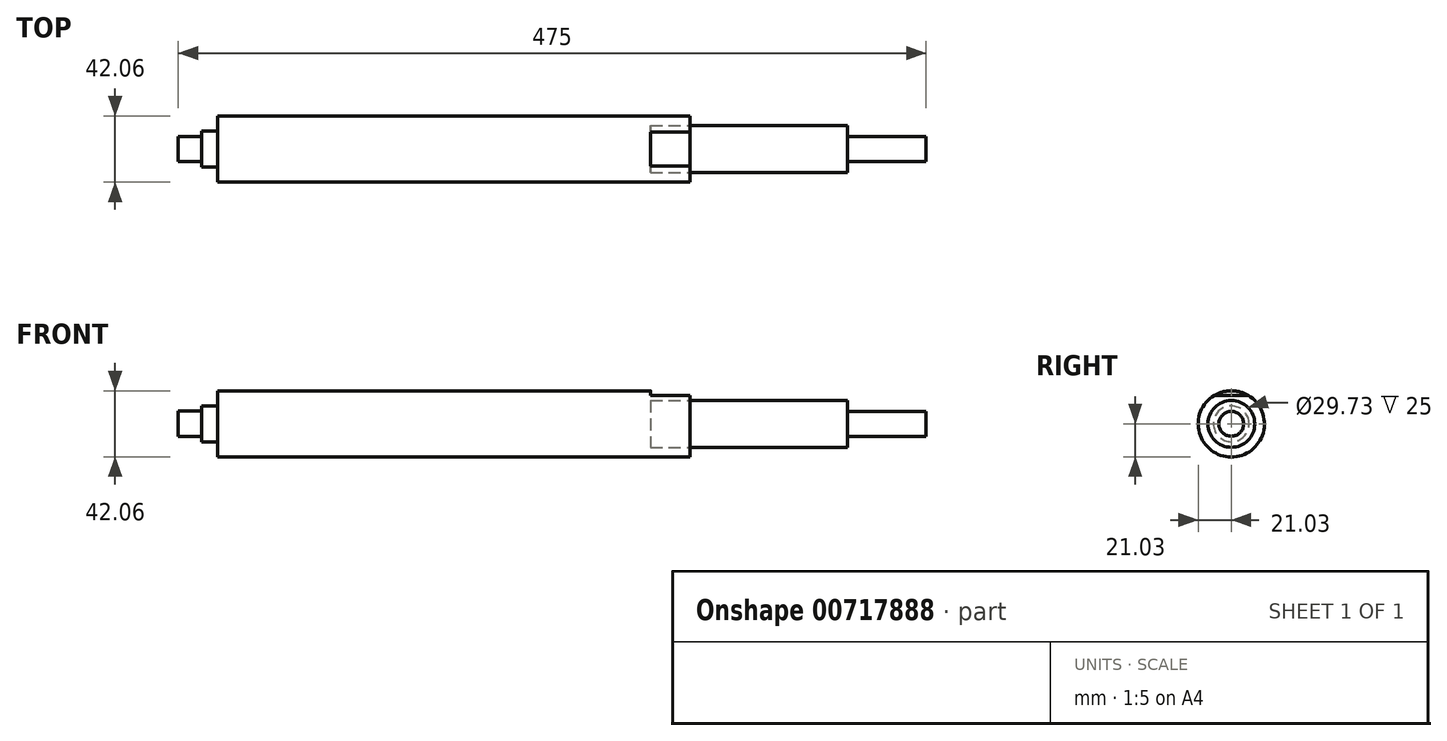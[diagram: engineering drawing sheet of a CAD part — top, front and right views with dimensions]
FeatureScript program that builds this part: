
annotation { "Feature Type Name" : "Feature", "Feature Type Description" : "" }
export const myFeature = defineFeature(function(context is Context, id is Id, definition is map)
    precondition{}
    {
        {
            var Q0;
            Q0=qCreatedBy(makeId("Front.planeOp"),FACE);
            var sketch = newSketch(context, id + "F0", { "sketchPlane" : qUnion([Q0])});
            skLineSegment(sketch, "E0", {"start": v(358.19, 0) * mm, "end": v(358.19, 7.88) * mm});
            skLineSegment(sketch, "E1", {"start": v(358.19, 7.88) * mm, "end": v(308.19, 7.88) * mm});
            skLineSegment(sketch, "E2", {"start": v(308.19, 7.88) * mm, "end": v(308.19, 14.87) * mm});
            skLineSegment(sketch, "E3", {"start": v(308.19, 14.87) * mm, "end": v(208.19, 14.87) * mm});
            skLineSegment(sketch, "E4", {"start": v(208.19, 14.87) * mm, "end": v(208.19, 21.03) * mm});
            skLineSegment(sketch, "E5", {"start": v(208.19, 21.03) * mm, "end": v(-91.81, 21.03) * mm});
            skLineSegment(sketch, "E6", {"start": v(-91.81, 21.03) * mm, "end": v(-91.81, 11.37) * mm});
            skLineSegment(sketch, "E7", {"start": v(-91.81, 11.37) * mm, "end": v(-101.81, 11.37) * mm});
            skLineSegment(sketch, "E8", {"start": v(-101.81, 11.37) * mm, "end": v(-101.81, 8.09) * mm});
            skLineSegment(sketch, "E9", {"start": v(-101.81, 8.09) * mm, "end": v(-116.81, 8.09) * mm});
            skLineSegment(sketch, "E10", {"start": v(-116.81, 8.09) * mm, "end": v(-116.81, 0) * mm});
            skLineSegment(sketch, "E11", {"start": v(-116.81, 0) * mm, "end": v(358.19, 0) * mm});
            skSolve(sketch);
        }
        {
            var Q0;
            Q0 = qSketchRegion(id + "F0", true);
            var Q1;
            Q1=sQuery(id+"F0.wireOp",EDGE,"E11");
            revolve(context, id + "F1", {"surfaceOperationType" : NewSurfaceOperationType.NEW, "entities" : qUnion([Q0]), "axis" : qUnion([Q1]), "revolveType" : RevolveType.FULL});
        }
        {
            var Q0;
            Q0=makeQuery(id+"F1.opRevolve","SWEPT_FACE",FACE,{"disambiguationData":[OSD([sQuery(id+"F0.wireOp",EDGE,"E4")])]});
            var sketch = newSketch(context, id + "F2", { "sketchPlane" : qUnion([Q0])});
            skLineSegment(sketch, "E12.bottom", {"start": v(41.9, 18.03) * mm, "end": v(-41.9, 18.03) * mm});
            skLineSegment(sketch, "E12.top", {"start": v(41.9, 27.34) * mm, "end": v(-41.9, 27.34) * mm});
            skLineSegment(sketch, "E12.left", {"start": v(41.9, 18.03) * mm, "end": v(41.9, 27.34) * mm});
            skLineSegment(sketch, "E12.right", {"start": v(-41.9, 18.03) * mm, "end": v(-41.9, 27.34) * mm});
            skPoint(sketch, "E12.middle", {"position": v(0, 22.69) * mm});
            skCircle(sketch, "E13.0", {"center": v(0, 0) * mm, "radius": 21.03 * mm});
            skSolve(sketch);
        }
        {
            var Q0;
            Q0=makeQuery(id+"F2.imprint","IMPRINT",FACE,{"disambiguationData":[TD([[makeQuery(id+"F2.imprint","IMPRINT",EDGE,{"derivedFrom":sQuery(id+"F2.wireOp",EDGE,"E12.top")}),1.0]])]});
            var Q1;
            Q1=makeQuery(id+"F2.imprint","IMPRINT",FACE,{"disambiguationData":[TD([[makeQuery(id+"F2.imprint","IMPRINT",EDGE,{"derivedFrom":makeQuery(id+"F1.opRevolve","SWEPT_EDGE",EDGE,{"disambiguationData":[OSD([sQuery(id+"F0.wireOp",EDGE,"E3"),sQuery(id+"F0.wireOp",EDGE,"E4")])]})}),-1.0]])]});
            var Q2;
            {var subQ0=sQuery(id+"F2.wireOp",EDGE,"E13.0");var subQ1=sQuery(id+"F2.wireOp",EDGE,"E12.bottom");var subQ2=makeQuery(id+"F2.imprint","INTERSECT",VERTEX,{"disambiguationData":[OD(0.0)],"derivedFrom":[subQ1,subQ0]});Q2=makeQuery(id+"F2.imprint","IMPRINT",FACE,{"disambiguationData":[TD([[makeQuery(id+"F2.imprint","IMPRINT",EDGE,{"disambiguationData":[TD([[subQ2,-1.0]])],"derivedFrom":subQ1}),-1.0]])]});}
            extrude(context, id + "F3", {"entities" : qUnion([Q0, Q1, Q2]), "operationType" : NewBodyOperationType.REMOVE, "oppositeDirection" : true, "depth" : 25 * mm, "offsetDistance" : 25 * mm});
        }
    });
